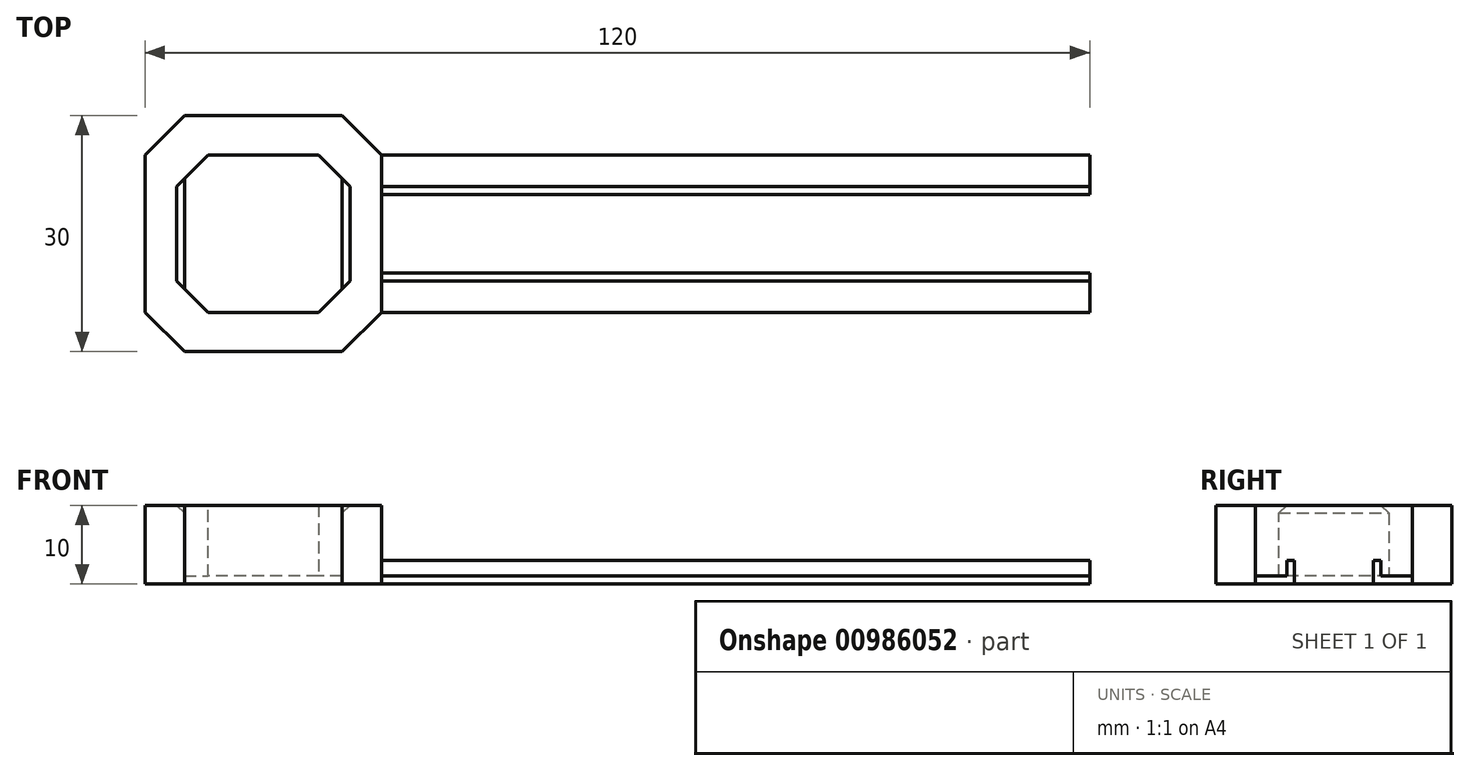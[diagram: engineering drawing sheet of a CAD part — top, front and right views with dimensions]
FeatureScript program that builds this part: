
annotation { "Feature Type Name" : "Feature", "Feature Type Description" : "" }
export const myFeature = defineFeature(function(context is Context, id is Id, definition is map)
    precondition{}
    {
        {
            var Q0;
            Q0=qCreatedBy(makeId("Top.planeOp"),FACE);
            var sketch = newSketch(context, id + "F0", { "sketchPlane" : qUnion([Q0])});
            skLineSegment(sketch, "E0.bottom", {"start": v(70, 10) * mm, "end": v(-70, 10) * mm});
            skLineSegment(sketch, "E0.top", {"start": v(70, -10) * mm, "end": v(-70, -10) * mm});
            skLineSegment(sketch, "E0.left", {"start": v(70, 10) * mm, "end": v(70, -10) * mm});
            skLineSegment(sketch, "E0.right", {"start": v(-70, 10) * mm, "end": v(-70, -10) * mm});
            skPoint(sketch, "E0.middle", {"position": v(0, 0) * mm});
            skLineSegment(sketch, "E1.bottom", {"start": v(70, 10) * mm, "end": v(50, 10) * mm});
            skLineSegment(sketch, "E1.top", {"start": v(70, -10) * mm, "end": v(50, -10) * mm});
            skLineSegment(sketch, "E1.right", {"start": v(50, 10) * mm, "end": v(50, -10) * mm});
            skLineSegment(sketch, "E2.bottom", {"start": v(-70, 10) * mm, "end": v(-30, 10) * mm});
            skLineSegment(sketch, "E3.bottom", {"start": v(-40, 5) * mm, "end": v(50, 5) * mm});
            skLineSegment(sketch, "E3.top", {"start": v(-40, -5) * mm, "end": v(50, -5) * mm});
            skLineSegment(sketch, "E3.left", {"start": v(-40, 5) * mm, "end": v(-40, -5) * mm});
            skLineSegment(sketch, "E3.right", {"start": v(50, 5) * mm, "end": v(50, -5) * mm});
            skLineSegment(sketch, "E4", {"start": v(-70, 10) * mm, "end": v(-70, 15) * mm});
            skLineSegment(sketch, "E5", {"start": v(-70, 15) * mm, "end": v(-40, 15) * mm});
            skLineSegment(sketch, "E6", {"start": v(-40, 15) * mm, "end": v(-40, -15) * mm});
            skLineSegment(sketch, "E7", {"start": v(-40, -15) * mm, "end": v(-70, -15) * mm});
            skLineSegment(sketch, "E8", {"start": v(-70, -15) * mm, "end": v(-70, -10) * mm});
            skLineSegment(sketch, "E9.bottom", {"start": v(-65, 10) * mm, "end": v(-45, 10) * mm});
            skLineSegment(sketch, "E9.top", {"start": v(-65, -10) * mm, "end": v(-45, -10) * mm});
            skLineSegment(sketch, "E9.left", {"start": v(-65, 10) * mm, "end": v(-65, -10) * mm});
            skLineSegment(sketch, "E9.right", {"start": v(-45, 10) * mm, "end": v(-45, -10) * mm});
            skSolve(sketch);
        }
        {
            var Q0;
            {var subQ5=sQuery(id+"F0.wireOp",EDGE,"E3.top");Q0=makeQuery(id+"F0.imprint","IMPRINT",FACE,{"disambiguationData":[TD([[makeQuery(id+"F0.imprint","IMPRINT",EDGE,{"derivedFrom":subQ5}),-1.0]])]});}
            var Q1;
            {var subQ1=sQuery(id+"F0.wireOp",EDGE,"E0.bottom");Q1=makeQuery(id+"F0.imprint","IMPRINT",FACE,{"disambiguationData":[TD([[makeQuery(id+"F0.imprint","IMPRINT",EDGE,{"derivedFrom":subQ1}),1.0]])]});}
            extrude(context, id + "F1", {"entities" : qUnion([Q0, Q1]), "depth" : 1 * mm, "offsetDistance" : 25 * mm});
        }
        {
            var Q0;
            {var subQ1=sQuery(id+"F0.wireOp",EDGE,"E1.bottom");Q0=makeQuery(id+"F0.imprint","IMPRINT",FACE,{"disambiguationData":[TD([[makeQuery(id+"F0.imprint","IMPRINT",EDGE,{"derivedFrom":subQ1}),1.0]])]});}
            var Q1;
            {var subQ1=sQuery(id+"F0.wireOp",EDGE,"E4");Q1=makeQuery(id+"F0.imprint","IMPRINT",FACE,{"disambiguationData":[TD([[makeQuery(id+"F0.imprint","IMPRINT",EDGE,{"derivedFrom":subQ1}),-1.0]])]});}
            var Q2;
            {var subQ5=sQuery(id+"F0.wireOp",EDGE,"E9.right");Q2=makeQuery(id+"F0.imprint","IMPRINT",FACE,{"disambiguationData":[TD([[makeQuery(id+"F0.imprint","IMPRINT",EDGE,{"derivedFrom":subQ5}),1.0]])]});}
            var Q3;
            {var subQ0=sQuery(id+"F0.wireOp",EDGE,"E0.right");Q3=makeQuery(id+"F0.imprint","IMPRINT",FACE,{"disambiguationData":[TD([[makeQuery(id+"F0.imprint","IMPRINT",EDGE,{"derivedFrom":subQ0}),1.0]])]});}
            var Q4;
            {var subQ0=sQuery(id+"F0.wireOp",EDGE,"E7");Q4=makeQuery(id+"F0.imprint","IMPRINT",FACE,{"disambiguationData":[TD([[makeQuery(id+"F0.imprint","IMPRINT",EDGE,{"derivedFrom":subQ0}),-1.0]])]});}
            extrude(context, id + "F2", {"entities" : qUnion([Q0, Q1, Q2, Q3, Q4]), "operationType" : NewBodyOperationType.ADD, "depth" : 10 * mm, "offsetDistance" : 25 * mm});
        }
        {
            var Q0;
            Q0=makeQuery(id+"F1.opExtrude","CAP_FACE",FACE,{"disambiguationData":[OSD([sQuery(id+"F0.wireOp",EDGE,"E0.top"),sQuery(id+"F0.wireOp",EDGE,"E1.right"),sQuery(id+"F0.wireOp",EDGE,"E3.top"),sQuery(id+"F0.wireOp",EDGE,"E6")])],"isStart":false});
            var sketch = newSketch(context, id + "F3", { "sketchPlane" : qUnion([Q0])});
            skLineSegment(sketch, "E10.0.0", {"start": v(50, 10) * mm, "end": v(-40, 10) * mm});
            skLineSegment(sketch, "E10.0.1", {"start": v(-40, 10) * mm, "end": v(-40, 5) * mm});
            skLineSegment(sketch, "E10.0.2", {"start": v(-40, 5) * mm, "end": v(50, 5) * mm});
            skLineSegment(sketch, "E10.0.3", {"start": v(50, 5) * mm, "end": v(50, 10) * mm});
            skLineSegment(sketch, "E11.0.0", {"start": v(-40, -10) * mm, "end": v(50, -10) * mm});
            skLineSegment(sketch, "E11.0.1", {"start": v(50, -10) * mm, "end": v(50, -5) * mm});
            skLineSegment(sketch, "E11.0.2", {"start": v(50, -5) * mm, "end": v(-40, -5) * mm});
            skLineSegment(sketch, "E11.0.3", {"start": v(-40, -5) * mm, "end": v(-40, -10) * mm});
            skLineSegment(sketch, "E12", {"start": v(-40, 6) * mm, "end": v(50, 6) * mm});
            skLineSegment(sketch, "E13", {"start": v(50, -6) * mm, "end": v(-40, -6) * mm});
            skSolve(sketch);
        }
        {
            var Q0;
            {var subQ0=sQuery(id+"F3.wireOp",EDGE,"E10.0.2");Q0=makeQuery(id+"F3.imprint","IMPRINT",FACE,{"disambiguationData":[TD([[makeQuery(id+"F3.imprint","IMPRINT",EDGE,{"derivedFrom":subQ0}),1.0]])]});}
            var Q1;
            {var subQ0=sQuery(id+"F3.wireOp",EDGE,"E11.0.2");Q1=makeQuery(id+"F3.imprint","IMPRINT",FACE,{"disambiguationData":[TD([[makeQuery(id+"F3.imprint","IMPRINT",EDGE,{"derivedFrom":subQ0}),-1.0]])]});}
            extrude(context, id + "F4", {"entities" : qUnion([Q0, Q1]), "operationType" : NewBodyOperationType.ADD, "depth" : 2 * mm, "offsetDistance" : 25 * mm});
        }
        {
            var Q0;
            Q0=makeQuery(id+"F2.opExtrude","SWEPT_EDGE",EDGE,{"disambiguationData":[OSD([sQuery(id+"F0.wireOp",EDGE,"E1.top"),sQuery(id+"F0.wireOp",EDGE,"E0.left")])]});
            var Q1;
            Q1=makeQuery(id+"F2.opExtrude","SWEPT_EDGE",EDGE,{"disambiguationData":[OSD([sQuery(id+"F0.wireOp",EDGE,"E1.bottom"),sQuery(id+"F0.wireOp",EDGE,"E0.left")])]});
            var Q2;
            Q2=makeQuery(id+"F2.opExtrude","SWEPT_EDGE",EDGE,{"disambiguationData":[OSD([sQuery(id+"F0.wireOp",EDGE,"E0.top"),sQuery(id+"F0.wireOp",EDGE,"E1.top"),sQuery(id+"F0.wireOp",EDGE,"E1.right")])]});
            var Q3;
            Q3=makeQuery(id+"F2.opExtrude","SWEPT_EDGE",EDGE,{"disambiguationData":[OSD([sQuery(id+"F0.wireOp",EDGE,"E0.bottom"),sQuery(id+"F0.wireOp",EDGE,"E1.bottom"),sQuery(id+"F0.wireOp",EDGE,"E1.right")])]});
            chamfer(context, id + "F5", {"entities" : qUnion([Q0, Q1, Q2, Q3]), "width" : 3 * mm, "tangentPropagation" : true});
        }
        {
            var Q0;
            Q0=makeQuery(id+"F2.opExtrude","CAP_EDGE",EDGE,{"disambiguationData":[OSD([sQuery(id+"F0.wireOp",EDGE,"E1.bottom")])],"isStart":false});
            var Q1;
            {var subQ0=sQuery(id+"F0.wireOp",EDGE,"E1.right");var subQ1=sQuery(id+"F0.wireOp",EDGE,"E1.bottom");Q1=makeQuery(id+"F5.opChamfer","BLEND_EDGE",EDGE,{"blendedFrom":[makeQuery(id+"F2.opExtrude","SWEPT_EDGE",EDGE,{"disambiguationData":[OSD([sQuery(id+"F0.wireOp",EDGE,"E0.bottom"),subQ1,subQ0])]}),makeQuery(id+"F2.opExtrude","CAP_FACE",FACE,{"disambiguationData":[OSD([subQ1,sQuery(id+"F0.wireOp",EDGE,"E1.top"),sQuery(id+"F0.wireOp",EDGE,"E0.left"),subQ0,sQuery(id+"F0.wireOp",EDGE,"E3.right")])],"isStart":false})],"blendedInto":[makeQuery(id+"F2.opExtrude","CAP_FACE",FACE,{"disambiguationData":[OSD([subQ1,sQuery(id+"F0.wireOp",EDGE,"E1.top"),sQuery(id+"F0.wireOp",EDGE,"E0.left"),subQ0,sQuery(id+"F0.wireOp",EDGE,"E3.right")])],"isStart":false})]});}
            var Q2;
            Q2=makeQuery(id+"F2.opExtrude","CAP_EDGE",EDGE,{"disambiguationData":[OSD([sQuery(id+"F0.wireOp",EDGE,"E1.right"),sQuery(id+"F0.wireOp",EDGE,"E3.right")])],"isStart":false});
            var Q3;
            {var subQ0=sQuery(id+"F0.wireOp",EDGE,"E1.right");var subQ1=sQuery(id+"F0.wireOp",EDGE,"E1.top");Q3=makeQuery(id+"F5.opChamfer","BLEND_EDGE",EDGE,{"blendedFrom":[makeQuery(id+"F2.opExtrude","SWEPT_EDGE",EDGE,{"disambiguationData":[OSD([sQuery(id+"F0.wireOp",EDGE,"E0.top"),subQ1,subQ0])]}),makeQuery(id+"F2.opExtrude","CAP_FACE",FACE,{"disambiguationData":[OSD([sQuery(id+"F0.wireOp",EDGE,"E1.bottom"),subQ1,sQuery(id+"F0.wireOp",EDGE,"E0.left"),subQ0,sQuery(id+"F0.wireOp",EDGE,"E3.right")])],"isStart":false})],"blendedInto":[makeQuery(id+"F2.opExtrude","CAP_FACE",FACE,{"disambiguationData":[OSD([sQuery(id+"F0.wireOp",EDGE,"E1.bottom"),subQ1,sQuery(id+"F0.wireOp",EDGE,"E0.left"),subQ0,sQuery(id+"F0.wireOp",EDGE,"E3.right")])],"isStart":false})]});}
            var Q4;
            Q4=makeQuery(id+"F2.opExtrude","CAP_EDGE",EDGE,{"disambiguationData":[OSD([sQuery(id+"F0.wireOp",EDGE,"E1.top")])],"isStart":false});
            var Q5;
            {var subQ0=sQuery(id+"F0.wireOp",EDGE,"E0.left");var subQ1=sQuery(id+"F0.wireOp",EDGE,"E1.top");Q5=makeQuery(id+"F5.opChamfer","BLEND_EDGE",EDGE,{"blendedFrom":[makeQuery(id+"F2.opExtrude","SWEPT_EDGE",EDGE,{"disambiguationData":[OSD([subQ1,subQ0])]}),makeQuery(id+"F2.opExtrude","CAP_FACE",FACE,{"disambiguationData":[OSD([sQuery(id+"F0.wireOp",EDGE,"E1.bottom"),subQ1,subQ0,sQuery(id+"F0.wireOp",EDGE,"E1.right"),sQuery(id+"F0.wireOp",EDGE,"E3.right")])],"isStart":false})],"blendedInto":[makeQuery(id+"F2.opExtrude","CAP_FACE",FACE,{"disambiguationData":[OSD([sQuery(id+"F0.wireOp",EDGE,"E1.bottom"),subQ1,subQ0,sQuery(id+"F0.wireOp",EDGE,"E1.right"),sQuery(id+"F0.wireOp",EDGE,"E3.right")])],"isStart":false})]});}
            var Q6;
            Q6=makeQuery(id+"F2.opExtrude","CAP_FACE",FACE,{"disambiguationData":[OSD([sQuery(id+"F0.wireOp",EDGE,"E1.bottom"),sQuery(id+"F0.wireOp",EDGE,"E1.top"),sQuery(id+"F0.wireOp",EDGE,"E0.left"),sQuery(id+"F0.wireOp",EDGE,"E1.right"),sQuery(id+"F0.wireOp",EDGE,"E3.right")])],"isStart":false});
            var Q7;
            Q7=makeQuery(id+"F2.opExtrude","CAP_EDGE",EDGE,{"disambiguationData":[OSD([sQuery(id+"F0.wireOp",EDGE,"E9.bottom")])],"isStart":false});
            var Q8;
            Q8=makeQuery(id+"F2.opExtrude","CAP_EDGE",EDGE,{"disambiguationData":[OSD([sQuery(id+"F0.wireOp",EDGE,"E9.left")])],"isStart":false});
            var Q9;
            Q9=makeQuery(id+"F2.opExtrude","CAP_EDGE",EDGE,{"disambiguationData":[OSD([sQuery(id+"F0.wireOp",EDGE,"E9.top")])],"isStart":false});
            var Q10;
            Q10=makeQuery(id+"F2.opExtrude","CAP_EDGE",EDGE,{"disambiguationData":[OSD([sQuery(id+"F0.wireOp",EDGE,"E9.right")])],"isStart":false});
            var Q11;
            Q11=makeQuery(id+"F2.opExtrude","CAP_EDGE",EDGE,{"disambiguationData":[OSD([sQuery(id+"F0.wireOp",EDGE,"E9.left")])],"isStart":true});
            var Q12;
            Q12=makeQuery(id+"F2.opExtrude","CAP_EDGE",EDGE,{"disambiguationData":[OSD([sQuery(id+"F0.wireOp",EDGE,"E9.top")])],"isStart":true});
            var Q13;
            Q13=makeQuery(id+"F2.opExtrude","CAP_EDGE",EDGE,{"disambiguationData":[OSD([sQuery(id+"F0.wireOp",EDGE,"E9.right")])],"isStart":true});
            var Q14;
            Q14=makeQuery(id+"F2.opExtrude","CAP_EDGE",EDGE,{"disambiguationData":[OSD([sQuery(id+"F0.wireOp",EDGE,"E9.bottom")])],"isStart":true});
            chamfer(context, id + "F6", {"entities" : qUnion([Q0, Q1, Q2, Q3, Q4, Q5, Q6, Q7, Q8, Q9, Q10, Q11, Q12, Q13, Q14]), "width" : 1 * mm, "tangentPropagation" : true});
        }
        {
            var Q0;
            Q0=makeQuery(id+"F2.opExtrude","SWEPT_EDGE",EDGE,{"disambiguationData":[OSD([sQuery(id+"F0.wireOp",EDGE,"E5"),sQuery(id+"F0.wireOp",EDGE,"E6")])]});
            var Q1;
            Q1=makeQuery(id+"F2.opExtrude","SWEPT_EDGE",EDGE,{"disambiguationData":[OSD([sQuery(id+"F0.wireOp",EDGE,"E4"),sQuery(id+"F0.wireOp",EDGE,"E5")])]});
            var Q2;
            Q2=makeQuery(id+"F2.opExtrude","SWEPT_EDGE",EDGE,{"disambiguationData":[OSD([sQuery(id+"F0.wireOp",EDGE,"E7"),sQuery(id+"F0.wireOp",EDGE,"E8")])]});
            var Q3;
            Q3=makeQuery(id+"F2.opExtrude","SWEPT_EDGE",EDGE,{"disambiguationData":[OSD([sQuery(id+"F0.wireOp",EDGE,"E6"),sQuery(id+"F0.wireOp",EDGE,"E7")])]});
            chamfer(context, id + "F7", {"entities" : qUnion([Q0, Q1, Q2, Q3]), "width" : 5 * mm, "tangentPropagation" : true});
        }
    });
